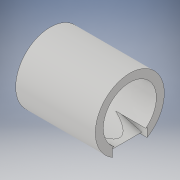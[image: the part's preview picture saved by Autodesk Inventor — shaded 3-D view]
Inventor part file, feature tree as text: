
AUTODESK INVENTOR PART (.ipt)
format: ipt  version: 2019 (Build 230136000, 136)  size: 126,976 bytes
history: native  units: in
note: dims shown in document units (in); Inventor stores cm internally (conversion verified against a paired STEP export)
features: sketch x2, plane x1, revolve x1, extrude x1
ambient origin geometry x8: Origin, YZ Plane, XZ Plane, XY Plane, X Axis, Y Axis, Z Axis, Center Point
bodies: Solid1 (feature_tree)
feature tree (5):
  plane  "Work Plane1"
  revolve  "Revolution1"  [1 undecoded]
  extrude  "Extrusion2"  TaperAngle=90.0deg  [1 undecoded]
  sketch  "Sketch2"  dims[d11=1.1811in d12=0.1181in]
  sketch  "Sketch3"  dims[d13=0.3937in d15=90.0deg d17=0.6693in d19=15.0deg d20=15.0deg d21=0.0984in d23=1.1024in d24=0.1969in d25=0.2091in d26=0.302in d27=0.5118in d28=0.0in]
note: 2 required parameter values undecoded (feature->parameter linkage not recoverable at this tier; creation-order binding heuristic only, values carry confidence <= 0.55)